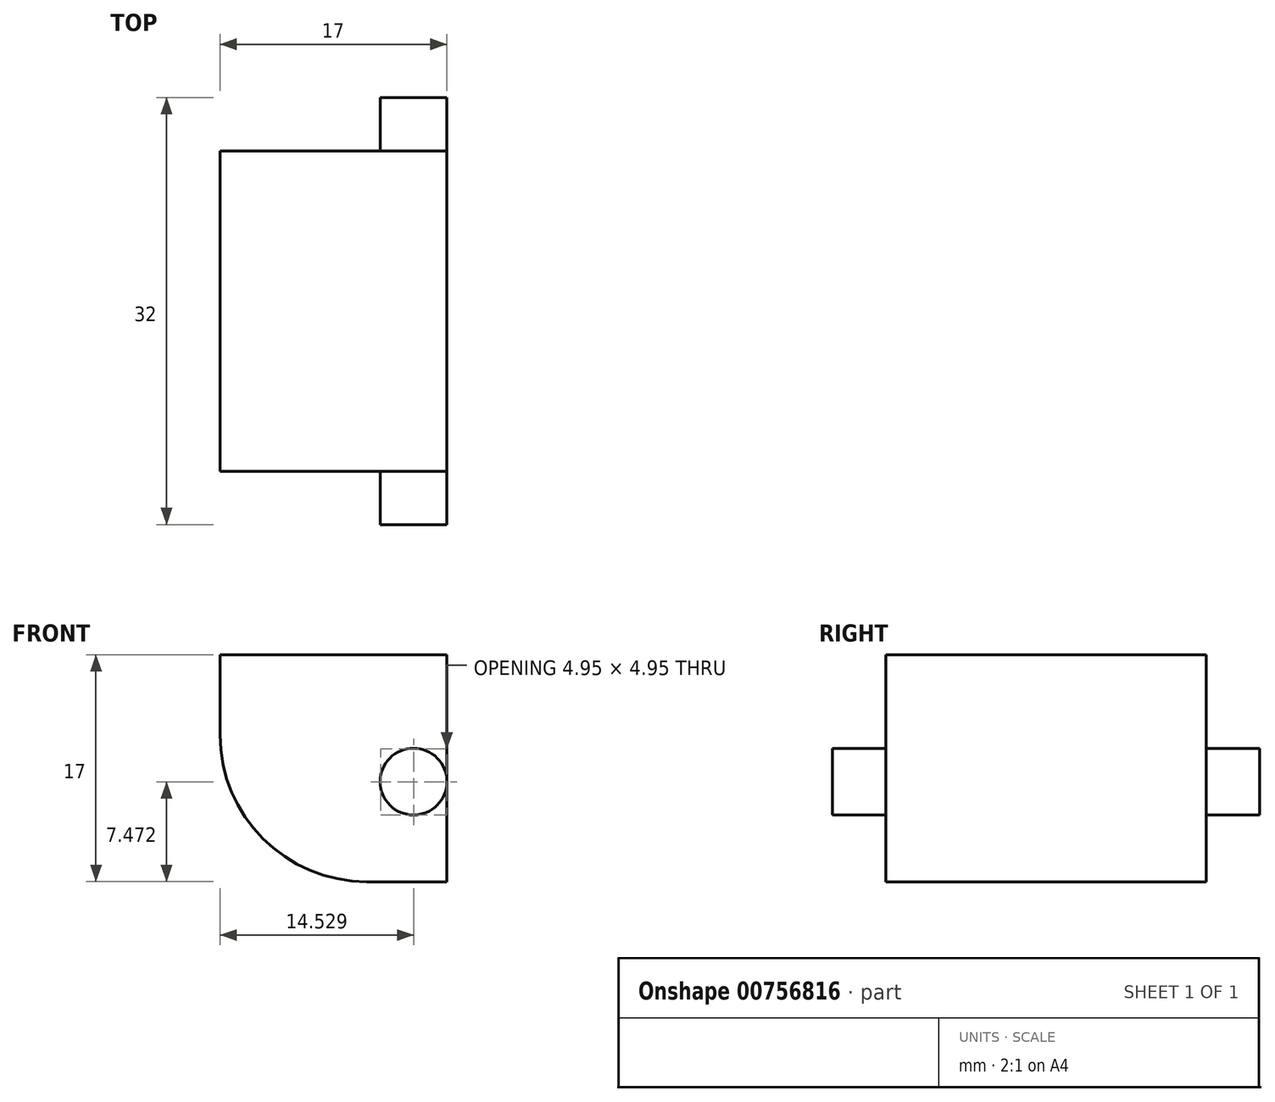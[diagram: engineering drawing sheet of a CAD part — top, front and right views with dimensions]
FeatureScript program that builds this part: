
annotation { "Feature Type Name" : "Feature", "Feature Type Description" : "" }
export const myFeature = defineFeature(function(context is Context, id is Id, definition is map)
    precondition{}
    {
        {
            var Q0;
            Q0=qCreatedBy(makeId("Front.planeOp"),FACE);
            var sketch = newSketch(context, id + "F0", { "sketchPlane" : qUnion([Q0])});
            skLineSegment(sketch, "E0.bottom", {"start": v(-54.7, 23.23) * mm, "end": v(-40.7, 23.23) * mm});
            skLineSegment(sketch, "E0.top", {"start": v(-54.7, 11.23) * mm, "end": v(-40.7, 11.23) * mm});
            skLineSegment(sketch, "E0.left", {"start": v(-54.7, 23.23) * mm, "end": v(-54.7, 11.23) * mm});
            skLineSegment(sketch, "E0.right", {"start": v(-40.7, 23.23) * mm, "end": v(-40.7, 11.23) * mm});
            skSolve(sketch);
        }
        {
            var Q0;
            Q0=makeQuery(id+"F0.imprint","IMPRINT",FACE,{"disambiguationData":[TD([[makeQuery(id+"F0.imprint","IMPRINT",EDGE,{"derivedFrom":sQuery(id+"F0.wireOp",EDGE,"E0.bottom")}),-1.0]])]});
            extrude(context, id + "F1", {"entities" : qUnion([Q0]), "depth" : (32 - 8) * mm, "offsetDistance" : 25 * mm});
        }
        {
            var Q0;
            Q0=makeQuery(id+"F1.opExtrude","CAP_FACE",FACE,{"disambiguationData":[OSD([sQuery(id+"F0.wireOp",EDGE,"E0.bottom"),sQuery(id+"F0.wireOp",EDGE,"E0.top"),sQuery(id+"F0.wireOp",EDGE,"E0.left"),sQuery(id+"F0.wireOp",EDGE,"E0.right")])],"isStart":false});
            var sketch = newSketch(context, id + "F2", { "sketchPlane" : qUnion([Q0])});
            skLineSegment(sketch, "E1.bottom", {"start": v(-40.7, 11.23) * mm, "end": v(-37.7, 11.23) * mm});
            skLineSegment(sketch, "E1.top", {"start": v(-40.7, 16.23) * mm, "end": v(-37.7, 16.23) * mm});
            skLineSegment(sketch, "E1.left", {"start": v(-40.7, 11.23) * mm, "end": v(-40.7, 16.23) * mm});
            skLineSegment(sketch, "E1.right", {"start": v(-37.7, 11.23) * mm, "end": v(-37.7, 16.23) * mm});
            skCircle(sketch, "E2", {"center": v(-40.2, 13.73) * mm, "radius": 2.5 * mm});
            skPoint(sketch, "E2.centerSnap0", {"position": v(-40.7, 13.73) * mm});
            skSolve(sketch);
        }
        {
            var Q0;
            {var subQ0=sQuery(id+"F2.wireOp",EDGE,"E2");var subQ2=sQuery(id+"F2.wireOp",EDGE,"E1.left");var subQ6=makeQuery(id+"F2.imprint","INTERSECT",VERTEX,{"disambiguationData":[OD(0.0)],"derivedFrom":[subQ2,subQ0]});Q0=makeQuery(id+"F2.imprint","IMPRINT",FACE,{"disambiguationData":[TD([[makeQuery(id+"F2.imprint","IMPRINT",EDGE,{"disambiguationData":[TD([[subQ6,-1.0]])],"derivedFrom":subQ2}),1.0]])]});}
            var Q1;
            {var subQ0=sQuery(id+"F2.wireOp",EDGE,"E2");var subQ1=sQuery(id+"F2.wireOp",EDGE,"E1.left");var subQ2=makeQuery(id+"F2.imprint","INTERSECT",VERTEX,{"disambiguationData":[OD(0.0)],"derivedFrom":[subQ1,subQ0]});Q1=makeQuery(id+"F2.imprint","IMPRINT",FACE,{"disambiguationData":[TD([[makeQuery(id+"F2.imprint","IMPRINT",EDGE,{"disambiguationData":[TD([[subQ2,-1.0]])],"derivedFrom":subQ1}),-1.0]])]});}
            extrude(context, id + "F3", {"entities" : qUnion([Q0, Q1]), "operationType" : NewBodyOperationType.ADD, "depth" : -(24 + 4) * mm, "offsetDistance" : 25 * mm});
        }
        {
            var Q0;
            {var subQ0=sQuery(id+"F2.wireOp",EDGE,"E2");var subQ2=sQuery(id+"F2.wireOp",EDGE,"E1.left");var subQ6=makeQuery(id+"F2.imprint","INTERSECT",VERTEX,{"disambiguationData":[OD(0.0)],"derivedFrom":[subQ2,subQ0]});Q0=makeQuery(id+"F2.imprint","IMPRINT",FACE,{"disambiguationData":[TD([[makeQuery(id+"F2.imprint","IMPRINT",EDGE,{"disambiguationData":[TD([[subQ6,-1.0]])],"derivedFrom":subQ2}),1.0]])]});}
            var Q1;
            {var subQ0=sQuery(id+"F2.wireOp",EDGE,"E2");var subQ1=sQuery(id+"F2.wireOp",EDGE,"E1.left");var subQ2=makeQuery(id+"F2.imprint","INTERSECT",VERTEX,{"disambiguationData":[OD(0.0)],"derivedFrom":[subQ1,subQ0]});Q1=makeQuery(id+"F2.imprint","IMPRINT",FACE,{"disambiguationData":[TD([[makeQuery(id+"F2.imprint","IMPRINT",EDGE,{"disambiguationData":[TD([[subQ2,-1.0]])],"derivedFrom":subQ1}),-1.0]])]});}
            extrude(context, id + "F4", {"entities" : qUnion([Q0, Q1]), "operationType" : NewBodyOperationType.ADD, "depth" : 4 * mm, "offsetDistance" : 25 * mm});
        }
        {
            var Q0;
            Q0=makeQuery(id+"F3.boolean.opBoolean","MERGE",FACE,{"derivedFrom":[makeQuery(id+"F1.opExtrude","CAP_FACE",FACE,{"disambiguationData":[OSD([sQuery(id+"F0.wireOp",EDGE,"E0.bottom"),sQuery(id+"F0.wireOp",EDGE,"E0.top"),sQuery(id+"F0.wireOp",EDGE,"E0.left"),sQuery(id+"F0.wireOp",EDGE,"E0.right")])],"isStart":false}),makeQuery(id+"F3.opExtrude","CAP_FACE",FACE,{"disambiguationData":[OSD([sQuery(id+"F2.wireOp",EDGE,"E2")])],"isStart":true})]});
            var sketch = newSketch(context, id + "F5", { "sketchPlane" : qUnion([Q0])});
            skLineSegment(sketch, "E3.bottom", {"start": v(-40.7, 23.23) * mm, "end": v(-37.7, 23.23) * mm});
            skLineSegment(sketch, "E3.top", {"start": v(-40.7, 13.23) * mm, "end": v(-37.7, 13.23) * mm});
            skLineSegment(sketch, "E3.left", {"start": v(-40.7, 23.23) * mm, "end": v(-40.7, 13.23) * mm});
            skLineSegment(sketch, "E3.right", {"start": v(-37.7, 23.23) * mm, "end": v(-37.7, 13.23) * mm});
            skSolve(sketch);
        }
        {
            var Q0;
            {var subQ3=sQuery(id+"F5.wireOp",EDGE,"E3.bottom");Q0=makeQuery(id+"F5.imprint","IMPRINT",FACE,{"disambiguationData":[TD([[makeQuery(id+"F5.imprint","IMPRINT",EDGE,{"derivedFrom":subQ3}),-1.0]])]});}
            extrude(context, id + "F6", {"entities" : qUnion([Q0]), "operationType" : NewBodyOperationType.ADD, "depth" : -24 * mm, "offsetDistance" : 25 * mm});
        }
        {
            var Q0;
            Q0=makeQuery(id+"F6.boolean.opBoolean","MERGE",FACE,{"derivedFrom":[makeQuery(id+"F3.boolean.opBoolean","MERGE",FACE,{"derivedFrom":[makeQuery(id+"F1.opExtrude","CAP_FACE",FACE,{"disambiguationData":[OSD([sQuery(id+"F0.wireOp",EDGE,"E0.bottom"),sQuery(id+"F0.wireOp",EDGE,"E0.top"),sQuery(id+"F0.wireOp",EDGE,"E0.left"),sQuery(id+"F0.wireOp",EDGE,"E0.right")])],"isStart":false}),makeQuery(id+"F3.opExtrude","CAP_FACE",FACE,{"disambiguationData":[OSD([sQuery(id+"F2.wireOp",EDGE,"E2")])],"isStart":true})]}),makeQuery(id+"F6.opExtrude","CAP_FACE",FACE,{"disambiguationData":[OSD([sQuery(id+"F5.wireOp",EDGE,"E3.bottom"),sQuery(id+"F5.wireOp",EDGE,"E3.top"),sQuery(id+"F5.wireOp",EDGE,"E3.left"),sQuery(id+"F5.wireOp",EDGE,"E3.right")])],"isStart":true})]});
            var sketch = newSketch(context, id + "F7", { "sketchPlane" : qUnion([Q0])});
            skLineSegment(sketch, "E4.bottom", {"start": v(-54.7, 23.23) * mm, "end": v(-37.7, 23.23) * mm});
            skLineSegment(sketch, "E4.top", {"start": v(-54.7, 6.23) * mm, "end": v(-37.7, 6.23) * mm});
            skLineSegment(sketch, "E4.left", {"start": v(-54.7, 23.23) * mm, "end": v(-54.7, 6.23) * mm});
            skLineSegment(sketch, "E4.right", {"start": v(-37.7, 23.23) * mm, "end": v(-37.7, 6.23) * mm});
            skSolve(sketch);
        }
        {
            var Q0;
            {var subQ10=sQuery(id+"F7.wireOp",EDGE,"E4.top");Q0=makeQuery(id+"F7.imprint","IMPRINT",FACE,{"disambiguationData":[TD([[makeQuery(id+"F7.imprint","IMPRINT",EDGE,{"derivedFrom":subQ10}),1.0]])]});}
            extrude(context, id + "F8", {"entities" : qUnion([Q0]), "operationType" : NewBodyOperationType.ADD, "depth" : -24 * mm, "offsetDistance" : 25 * mm});
        }
        {
            var Q0;
            Q0=makeQuery(id+"F8.opExtrude","SWEPT_EDGE",EDGE,{"disambiguationData":[OSD([sQuery(id+"F7.wireOp",EDGE,"E4.top"),sQuery(id+"F7.wireOp",EDGE,"E4.left")])]});
            fillet(context, id + "F9", {"entities" : qUnion([Q0]), "radius" : (17 - 6) * mm, "tangentPropagation" : true, "allowEdgeOverflow" : false});
        }
    });
